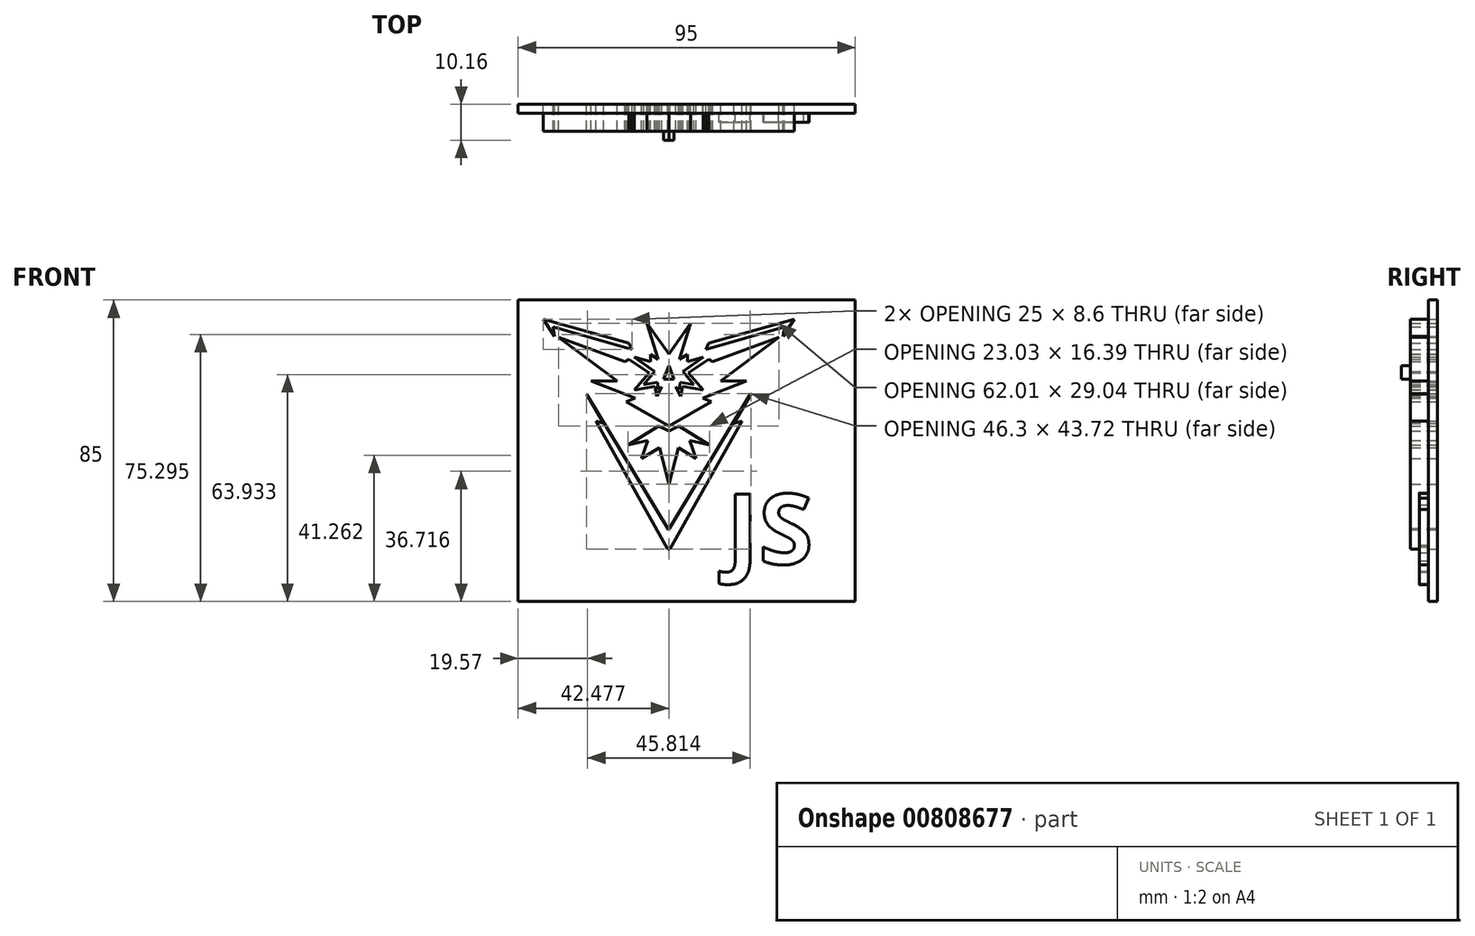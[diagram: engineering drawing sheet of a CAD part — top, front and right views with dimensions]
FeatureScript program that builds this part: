
annotation { "Feature Type Name" : "Feature", "Feature Type Description" : "" }
export const myFeature = defineFeature(function(context is Context, id is Id, definition is map)
    precondition{}
    {
        {
            var Q0;
            Q0=qCreatedBy(makeId("Front.planeOp"),FACE);
            var sketch = newSketch(context, id + "F0", { "sketchPlane" : qUnion([Q0])});
            skLineSegment(sketch, "E0", {"start": v(1.5, 35.4) * mm, "end": v(-4.67, 44.05) * mm});
            skLineSegment(sketch, "E1", {"start": v(-4.67, 44.05) * mm, "end": v(-1.5, 33.83) * mm});
            skLineSegment(sketch, "E2", {"start": v(-1.5, 33.83) * mm, "end": v(-3.69, 35.28) * mm});
            skLineSegment(sketch, "E3", {"start": v(-3.69, 35.28) * mm, "end": v(-3.69, 33.23) * mm});
            skLineSegment(sketch, "E4", {"start": v(-3.69, 33.23) * mm, "end": v(-8.18, 34.47) * mm});
            skLineSegment(sketch, "E5", {"start": v(-8.18, 34.47) * mm, "end": v(-2.45, 30.4) * mm});
            skLineSegment(sketch, "E6", {"start": v(-2.45, 30.4) * mm, "end": v(-5.53, 26.76) * mm});
            skLineSegment(sketch, "E7", {"start": v(-5.53, 26.76) * mm, "end": v(-1.76, 27.4) * mm});
            skLineSegment(sketch, "E8", {"start": v(-1.76, 27.4) * mm, "end": v(-1.42, 25.4) * mm});
            skLineSegment(sketch, "E9", {"start": v(-1.42, 25.4) * mm, "end": v(-0.44, 26.12) * mm});
            skLineSegment(sketch, "E10", {"start": v(-0.44, 26.12) * mm, "end": v(-1.85, 23.47) * mm});
            skLineSegment(sketch, "E11", {"start": v(-1.85, 23.47) * mm, "end": v(-2.32, 26.25) * mm});
            skLineSegment(sketch, "E12", {"start": v(-2.32, 26.25) * mm, "end": v(-8.22, 25.25) * mm});
            skLineSegment(sketch, "E13", {"start": v(-8.22, 25.25) * mm, "end": v(-4.03, 30.06) * mm});
            skLineSegment(sketch, "E14", {"start": v(-4.03, 30.06) * mm, "end": v(-9.72, 33.91) * mm});
            skLineSegment(sketch, "E15", {"start": v(-9.72, 33.91) * mm, "end": v(-10.88, 33.23) * mm});
            skLineSegment(sketch, "E16", {"start": v(-10.88, 33.23) * mm, "end": v(-29.5, 40.03) * mm});
            skLineSegment(sketch, "E17", {"start": v(-29.5, 40.03) * mm, "end": v(-13.1, 27.7) * mm});
            skLineSegment(sketch, "E18", {"start": v(-13.1, 27.7) * mm, "end": v(-20.38, 27.7) * mm});
            skLineSegment(sketch, "E19", {"start": v(-20.38, 27.7) * mm, "end": v(-8.01, 22.95) * mm});
            skLineSegment(sketch, "E20", {"start": v(-8.01, 22.95) * mm, "end": v(-10.5, 21.93) * mm});
            skLineSegment(sketch, "E21", {"start": v(-10.5, 21.93) * mm, "end": v(1.5, 15.01) * mm});
            skLineSegment(sketch, "E22", {"start": v(-1.35, 15.06) * mm, "end": v(-10.01, 9.67) * mm});
            skLineSegment(sketch, "E23", {"start": v(-10.01, 9.67) * mm, "end": v(-4.38, 10.97) * mm});
            skLineSegment(sketch, "E24", {"start": v(-4.38, 10.97) * mm, "end": v(-6.2, 5.95) * mm});
            skLineSegment(sketch, "E25", {"start": v(-6.2, 5.95) * mm, "end": v(-1.17, 8.91) * mm});
            skLineSegment(sketch, "E26", {"start": v(-1.17, 8.91) * mm, "end": v(1.5, -1.33) * mm});
            skLineSegment(sketch, "E27", {"start": v(-1.35, 15.06) * mm, "end": v(1.5, 13.7) * mm});
            skLineSegment(sketch, "E28", {"start": v(-33.9, 45.2) * mm, "end": v(-30.64, 40.35) * mm});
            skLineSegment(sketch, "E29", {"start": v(-30.64, 40.35) * mm, "end": v(-31.05, 43.05) * mm});
            skLineSegment(sketch, "E30", {"start": v(-31.05, 43.05) * mm, "end": v(-8.9, 36.6) * mm});
            skLineSegment(sketch, "E31", {"start": v(-8.9, 36.6) * mm, "end": v(-9.75, 38.47) * mm});
            skLineSegment(sketch, "E32", {"start": v(-9.75, 38.47) * mm, "end": v(-33.9, 45.2) * mm});
            skLineSegment(sketch, "E33", {"start": v(-21.64, 24.13) * mm, "end": v(-16.86, 15.86) * mm});
            skLineSegment(sketch, "E34", {"start": v(-16.86, 15.86) * mm, "end": v(-19.05, 16.5) * mm});
            skLineSegment(sketch, "E35", {"start": v(-19.05, 16.5) * mm, "end": v(1.24, -19.55) * mm});
            skLineSegment(sketch, "E36", {"start": v(-21.64, 24.13) * mm, "end": v(1.24, -13.77) * mm});
            skLineSegment(sketch, "E37.MirrorCS", {"start": v(22.07, 16.5) * mm, "end": v(1.78, -19.55) * mm});
            skLineSegment(sketch, "E38.MirrorCS", {"start": v(24.59, 24.18) * mm, "end": v(1.7, -13.72) * mm});
            skLineSegment(sketch, "E39.MirrorCS", {"start": v(19.88, 15.86) * mm, "end": v(22.07, 16.5) * mm});
            skLineSegment(sketch, "E40.MirrorCS", {"start": v(24.66, 24.13) * mm, "end": v(19.88, 15.86) * mm});
            skLineSegment(sketch, "E41.MirrorCS", {"start": v(4.37, 15.06) * mm, "end": v(13.02, 9.67) * mm});
            skLineSegment(sketch, "E42.MirrorCS", {"start": v(13.02, 9.67) * mm, "end": v(7.4, 10.97) * mm});
            skLineSegment(sketch, "E43.MirrorCS", {"start": v(9.21, 5.95) * mm, "end": v(4.19, 8.91) * mm});
            skLineSegment(sketch, "E44.MirrorCS", {"start": v(7.4, 10.97) * mm, "end": v(9.21, 5.95) * mm});
            skLineSegment(sketch, "E45.MirrorCS", {"start": v(4.19, 8.91) * mm, "end": v(1.5, -1.33) * mm});
            skLineSegment(sketch, "E46.MirrorCS", {"start": v(4.37, 15.06) * mm, "end": v(1.5, 13.7) * mm});
            skLineSegment(sketch, "E47.MirrorCS", {"start": v(13.5, 21.93) * mm, "end": v(1.5, 15.01) * mm});
            skLineSegment(sketch, "E48.MirrorCS", {"start": v(11.03, 22.95) * mm, "end": v(13.5, 21.93) * mm});
            skLineSegment(sketch, "E49.MirrorCS", {"start": v(23.4, 27.7) * mm, "end": v(11.03, 22.95) * mm});
            skLineSegment(sketch, "E50.MirrorCS", {"start": v(16.12, 27.7) * mm, "end": v(23.4, 27.7) * mm});
            skLineSegment(sketch, "E51.MirrorCS", {"start": v(32.51, 40.03) * mm, "end": v(16.12, 27.7) * mm});
            skLineSegment(sketch, "E52.MirrorCS", {"start": v(13.9, 33.23) * mm, "end": v(32.51, 40.03) * mm});
            skLineSegment(sketch, "E53.MirrorCS", {"start": v(12.74, 33.91) * mm, "end": v(13.9, 33.23) * mm});
            skLineSegment(sketch, "E54.MirrorCS", {"start": v(7.05, 30.06) * mm, "end": v(12.74, 33.91) * mm});
            skLineSegment(sketch, "E55.MirrorCS", {"start": v(11.24, 25.25) * mm, "end": v(7.05, 30.06) * mm});
            skLineSegment(sketch, "E56.MirrorCS", {"start": v(5.33, 26.25) * mm, "end": v(11.24, 25.25) * mm});
            skLineSegment(sketch, "E57.MirrorCS", {"start": v(4.86, 23.47) * mm, "end": v(5.33, 26.25) * mm});
            skLineSegment(sketch, "E58.MirrorCS", {"start": v(3.45, 26.12) * mm, "end": v(4.86, 23.47) * mm});
            skLineSegment(sketch, "E59.MirrorCS", {"start": v(4.44, 25.4) * mm, "end": v(3.45, 26.12) * mm});
            skLineSegment(sketch, "E60.MirrorCS", {"start": v(4.78, 27.4) * mm, "end": v(4.44, 25.4) * mm});
            skLineSegment(sketch, "E61.MirrorCS", {"start": v(8.54, 26.76) * mm, "end": v(4.78, 27.4) * mm});
            skLineSegment(sketch, "E62.MirrorCS", {"start": v(5.46, 30.4) * mm, "end": v(8.54, 26.76) * mm});
            skLineSegment(sketch, "E63.MirrorCS", {"start": v(11.2, 34.47) * mm, "end": v(5.46, 30.4) * mm});
            skLineSegment(sketch, "E64.MirrorCS", {"start": v(6.7, 33.23) * mm, "end": v(11.2, 34.47) * mm});
            skLineSegment(sketch, "E65.MirrorCS", {"start": v(6.7, 35.28) * mm, "end": v(6.7, 33.23) * mm});
            skLineSegment(sketch, "E66.MirrorCS", {"start": v(4.52, 33.83) * mm, "end": v(6.7, 35.28) * mm});
            skLineSegment(sketch, "E67.MirrorCS", {"start": v(7.69, 44.05) * mm, "end": v(4.52, 33.83) * mm});
            skLineSegment(sketch, "E68.MirrorCS", {"start": v(1.5, 35.4) * mm, "end": v(7.69, 44.05) * mm});
            skLineSegment(sketch, "E69.MirrorCS", {"start": v(34.06, 43.05) * mm, "end": v(11.91, 36.6) * mm});
            skLineSegment(sketch, "E70.MirrorCS", {"start": v(12.76, 38.47) * mm, "end": v(36.91, 45.2) * mm});
            skLineSegment(sketch, "E71.MirrorCS", {"start": v(11.91, 36.6) * mm, "end": v(12.76, 38.47) * mm});
            skLineSegment(sketch, "E72.MirrorCS", {"start": v(33.65, 40.35) * mm, "end": v(34.06, 43.05) * mm});
            skLineSegment(sketch, "E73.MirrorCS", {"start": v(36.91, 45.2) * mm, "end": v(33.65, 40.35) * mm});
            skLineSegment(sketch, "E74", {"start": v(1.24, -13.77) * mm, "end": v(1.47, -14.16) * mm});
            skLineSegment(sketch, "E75", {"start": v(1.47, -14.16) * mm, "end": v(1.7, -13.72) * mm});
            skLineSegment(sketch, "E76", {"start": v(1.24, -19.55) * mm, "end": v(1.78, -19.55) * mm});
            skLineSegment(sketch, "E77", {"start": v(24.59, 24.18) * mm, "end": v(24.66, 24.13) * mm});
            skLineSegment(sketch, "E78.bottom", {"start": v(-40.97, 50.6) * mm, "end": v(54.03, 50.6) * mm});
            skLineSegment(sketch, "E78.top", {"start": v(-40.97, -34.4) * mm, "end": v(54.03, -34.4) * mm});
            skLineSegment(sketch, "E78.left", {"start": v(-40.97, 50.6) * mm, "end": v(-40.97, -34.4) * mm});
            skLineSegment(sketch, "E78.right", {"start": v(54.03, 50.6) * mm, "end": v(54.03, -34.4) * mm});
            skSolve(sketch);
        }
        {
            var Q0;
            Q0=makeQuery(id+"F0.imprint","IMPRINT",FACE,{"disambiguationData":[TD([[makeQuery(id+"F0.imprint","IMPRINT",EDGE,{"derivedFrom":sQuery(id+"F0.wireOp",EDGE,"E69.MirrorCS")}),-1.0]])]});
            var Q1;
            Q1=makeQuery(id+"F0.imprint","IMPRINT",FACE,{"disambiguationData":[TD([[makeQuery(id+"F0.imprint","IMPRINT",EDGE,{"derivedFrom":sQuery(id+"F0.wireOp",EDGE,"E33")}),1.0]])]});
            var Q2;
            Q2=makeQuery(id+"F0.imprint","IMPRINT",FACE,{"disambiguationData":[TD([[makeQuery(id+"F0.imprint","IMPRINT",EDGE,{"derivedFrom":sQuery(id+"F0.wireOp",EDGE,"E22")}),1.0]])]});
            var Q3;
            Q3=makeQuery(id+"F0.imprint","IMPRINT",FACE,{"disambiguationData":[TD([[makeQuery(id+"F0.imprint","IMPRINT",EDGE,{"derivedFrom":sQuery(id+"F0.wireOp",EDGE,"E28")}),1.0]])]});
            var Q4;
            Q4=makeQuery(id+"F0.imprint","IMPRINT",FACE,{"disambiguationData":[TD([[makeQuery(id+"F0.imprint","IMPRINT",EDGE,{"derivedFrom":sQuery(id+"F0.wireOp",EDGE,"E0")}),1.0]])]});
            extrude(context, id + "F1", {"entities" : qUnion([Q0, Q1, Q2, Q3, Q4]), "depth" : 7.62 * mm});
        }
        {
            var Q0;
            Q0 = qSketchRegion(id + "F0", true);
            extrude(context, id + "F2", {"entities" : qUnion([Q0]), "depth" : 2.54 * mm, "offsetDistance" : 25 * mm});
        }
        {
            var Q0;
            Q0=makeQuery(id+"F2.opExtrude","CAP_FACE",FACE,{"disambiguationData":[OSD([sQuery(id+"F0.wireOp",EDGE,"E0"),sQuery(id+"F0.wireOp",EDGE,"E1"),sQuery(id+"F0.wireOp",EDGE,"E2"),sQuery(id+"F0.wireOp",EDGE,"E3"),sQuery(id+"F0.wireOp",EDGE,"E4"),sQuery(id+"F0.wireOp",EDGE,"E5"),sQuery(id+"F0.wireOp",EDGE,"E6"),sQuery(id+"F0.wireOp",EDGE,"E7"),sQuery(id+"F0.wireOp",EDGE,"E8"),sQuery(id+"F0.wireOp",EDGE,"E9"),sQuery(id+"F0.wireOp",EDGE,"E10"),sQuery(id+"F0.wireOp",EDGE,"E11"),sQuery(id+"F0.wireOp",EDGE,"E12"),sQuery(id+"F0.wireOp",EDGE,"E13"),sQuery(id+"F0.wireOp",EDGE,"E14"),sQuery(id+"F0.wireOp",EDGE,"E15"),sQuery(id+"F0.wireOp",EDGE,"E16"),sQuery(id+"F0.wireOp",EDGE,"E17"),sQuery(id+"F0.wireOp",EDGE,"E18"),sQuery(id+"F0.wireOp",EDGE,"E19"),sQuery(id+"F0.wireOp",EDGE,"E20"),sQuery(id+"F0.wireOp",EDGE,"E21"),sQuery(id+"F0.wireOp",EDGE,"E22"),sQuery(id+"F0.wireOp",EDGE,"E23"),sQuery(id+"F0.wireOp",EDGE,"E24"),sQuery(id+"F0.wireOp",EDGE,"E25"),sQuery(id+"F0.wireOp",EDGE,"E26"),sQuery(id+"F0.wireOp",EDGE,"E27"),sQuery(id+"F0.wireOp",EDGE,"E28"),sQuery(id+"F0.wireOp",EDGE,"E29"),sQuery(id+"F0.wireOp",EDGE,"E30"),sQuery(id+"F0.wireOp",EDGE,"E31"),sQuery(id+"F0.wireOp",EDGE,"E32"),sQuery(id+"F0.wireOp",EDGE,"E33"),sQuery(id+"F0.wireOp",EDGE,"E34"),sQuery(id+"F0.wireOp",EDGE,"E35"),sQuery(id+"F0.wireOp",EDGE,"E36"),sQuery(id+"F0.wireOp",EDGE,"E37.MirrorCS"),sQuery(id+"F0.wireOp",EDGE,"E38.MirrorCS"),sQuery(id+"F0.wireOp",EDGE,"E39.MirrorCS"),sQuery(id+"F0.wireOp",EDGE,"E40.MirrorCS"),sQuery(id+"F0.wireOp",EDGE,"E41.MirrorCS"),sQuery(id+"F0.wireOp",EDGE,"E42.MirrorCS"),sQuery(id+"F0.wireOp",EDGE,"E43.MirrorCS"),sQuery(id+"F0.wireOp",EDGE,"E44.MirrorCS"),sQuery(id+"F0.wireOp",EDGE,"E45.MirrorCS"),sQuery(id+"F0.wireOp",EDGE,"E46.MirrorCS"),sQuery(id+"F0.wireOp",EDGE,"E47.MirrorCS"),sQuery(id+"F0.wireOp",EDGE,"E48.MirrorCS"),sQuery(id+"F0.wireOp",EDGE,"E49.MirrorCS"),sQuery(id+"F0.wireOp",EDGE,"E50.MirrorCS"),sQuery(id+"F0.wireOp",EDGE,"E51.MirrorCS"),sQuery(id+"F0.wireOp",EDGE,"E52.MirrorCS"),sQuery(id+"F0.wireOp",EDGE,"E53.MirrorCS"),sQuery(id+"F0.wireOp",EDGE,"E54.MirrorCS"),sQuery(id+"F0.wireOp",EDGE,"E55.MirrorCS"),sQuery(id+"F0.wireOp",EDGE,"E56.MirrorCS"),sQuery(id+"F0.wireOp",EDGE,"E57.MirrorCS"),sQuery(id+"F0.wireOp",EDGE,"E58.MirrorCS"),sQuery(id+"F0.wireOp",EDGE,"E59.MirrorCS"),sQuery(id+"F0.wireOp",EDGE,"E60.MirrorCS"),sQuery(id+"F0.wireOp",EDGE,"E61.MirrorCS"),sQuery(id+"F0.wireOp",EDGE,"E62.MirrorCS"),sQuery(id+"F0.wireOp",EDGE,"E63.MirrorCS"),sQuery(id+"F0.wireOp",EDGE,"E64.MirrorCS"),sQuery(id+"F0.wireOp",EDGE,"E65.MirrorCS"),sQuery(id+"F0.wireOp",EDGE,"E66.MirrorCS"),sQuery(id+"F0.wireOp",EDGE,"E67.MirrorCS"),sQuery(id+"F0.wireOp",EDGE,"E68.MirrorCS"),sQuery(id+"F0.wireOp",EDGE,"E69.MirrorCS"),sQuery(id+"F0.wireOp",EDGE,"E70.MirrorCS"),sQuery(id+"F0.wireOp",EDGE,"E71.MirrorCS"),sQuery(id+"F0.wireOp",EDGE,"E72.MirrorCS"),sQuery(id+"F0.wireOp",EDGE,"E73.MirrorCS"),sQuery(id+"F0.wireOp",EDGE,"E74"),sQuery(id+"F0.wireOp",EDGE,"E75"),sQuery(id+"F0.wireOp",EDGE,"E76"),sQuery(id+"F0.wireOp",EDGE,"E77"),sQuery(id+"F0.wireOp",EDGE,"E78.bottom"),sQuery(id+"F0.wireOp",EDGE,"E78.top"),sQuery(id+"F0.wireOp",EDGE,"E78.left"),sQuery(id+"F0.wireOp",EDGE,"E78.right")])],"isStart":false});
            var sketch = newSketch(context, id + "F3", { "sketchPlane" : qUnion([Q0])});
            skText(sketch, "E79", { "text": "JS", "fontName": "OpenSans-Bold.ttf"});
            const initialGuessF3  = {"E79": [0.01775, -0.02382, 1, 0, 0.01987]};
            skSetInitialGuess(sketch, initialGuessF3);
            skSolve(sketch);
        }
        {
            var Q0;
            Q0 = qSketchRegion(id + "F3", true);
            extrude(context, id + "F4", {"entities" : qUnion([Q0]), "operationType" : NewBodyOperationType.ADD, "depth" : 2.54 * mm, "offsetDistance" : 25 * mm});
        }
        {
            var Q0;
            Q0=makeQuery(id+"F1.opExtrude","CAP_FACE",FACE,{"disambiguationData":[OSD([sQuery(id+"F0.wireOp",EDGE,"E0"),sQuery(id+"F0.wireOp",EDGE,"E1"),sQuery(id+"F0.wireOp",EDGE,"E2"),sQuery(id+"F0.wireOp",EDGE,"E3"),sQuery(id+"F0.wireOp",EDGE,"E4"),sQuery(id+"F0.wireOp",EDGE,"E5"),sQuery(id+"F0.wireOp",EDGE,"E6"),sQuery(id+"F0.wireOp",EDGE,"E7"),sQuery(id+"F0.wireOp",EDGE,"E8"),sQuery(id+"F0.wireOp",EDGE,"E9"),sQuery(id+"F0.wireOp",EDGE,"E10"),sQuery(id+"F0.wireOp",EDGE,"E11"),sQuery(id+"F0.wireOp",EDGE,"E12"),sQuery(id+"F0.wireOp",EDGE,"E13"),sQuery(id+"F0.wireOp",EDGE,"E14"),sQuery(id+"F0.wireOp",EDGE,"E15"),sQuery(id+"F0.wireOp",EDGE,"E16"),sQuery(id+"F0.wireOp",EDGE,"E17"),sQuery(id+"F0.wireOp",EDGE,"E18"),sQuery(id+"F0.wireOp",EDGE,"E19"),sQuery(id+"F0.wireOp",EDGE,"E20"),sQuery(id+"F0.wireOp",EDGE,"E21"),sQuery(id+"F0.wireOp",EDGE,"E47.MirrorCS"),sQuery(id+"F0.wireOp",EDGE,"E48.MirrorCS"),sQuery(id+"F0.wireOp",EDGE,"E49.MirrorCS"),sQuery(id+"F0.wireOp",EDGE,"E50.MirrorCS"),sQuery(id+"F0.wireOp",EDGE,"E51.MirrorCS"),sQuery(id+"F0.wireOp",EDGE,"E52.MirrorCS"),sQuery(id+"F0.wireOp",EDGE,"E53.MirrorCS"),sQuery(id+"F0.wireOp",EDGE,"E54.MirrorCS"),sQuery(id+"F0.wireOp",EDGE,"E55.MirrorCS"),sQuery(id+"F0.wireOp",EDGE,"E56.MirrorCS"),sQuery(id+"F0.wireOp",EDGE,"E57.MirrorCS"),sQuery(id+"F0.wireOp",EDGE,"E58.MirrorCS"),sQuery(id+"F0.wireOp",EDGE,"E59.MirrorCS"),sQuery(id+"F0.wireOp",EDGE,"E60.MirrorCS"),sQuery(id+"F0.wireOp",EDGE,"E61.MirrorCS"),sQuery(id+"F0.wireOp",EDGE,"E62.MirrorCS"),sQuery(id+"F0.wireOp",EDGE,"E63.MirrorCS"),sQuery(id+"F0.wireOp",EDGE,"E64.MirrorCS"),sQuery(id+"F0.wireOp",EDGE,"E65.MirrorCS"),sQuery(id+"F0.wireOp",EDGE,"E66.MirrorCS"),sQuery(id+"F0.wireOp",EDGE,"E67.MirrorCS"),sQuery(id+"F0.wireOp",EDGE,"E68.MirrorCS")])],"isStart":false});
            var sketch = newSketch(context, id + "F5", { "sketchPlane" : qUnion([Q0])});
            skLineSegment(sketch, "E80", {"start": v(1.5, 32.03) * mm, "end": v(0, 28.33) * mm});
            skLineSegment(sketch, "E81", {"start": v(0, 28.33) * mm, "end": v(3, 28.33) * mm});
            skLineSegment(sketch, "E82", {"start": v(3, 28.33) * mm, "end": v(1.5, 32.03) * mm});
            skSolve(sketch);
        }
        {
            var Q0;
            Q0 = qSketchRegion(id + "F5", true);
            extrude(context, id + "F6", {"entities" : qUnion([Q0]), "operationType" : NewBodyOperationType.ADD, "depth" : 2.54 * mm, "offsetDistance" : 25 * mm});
        }
    });
